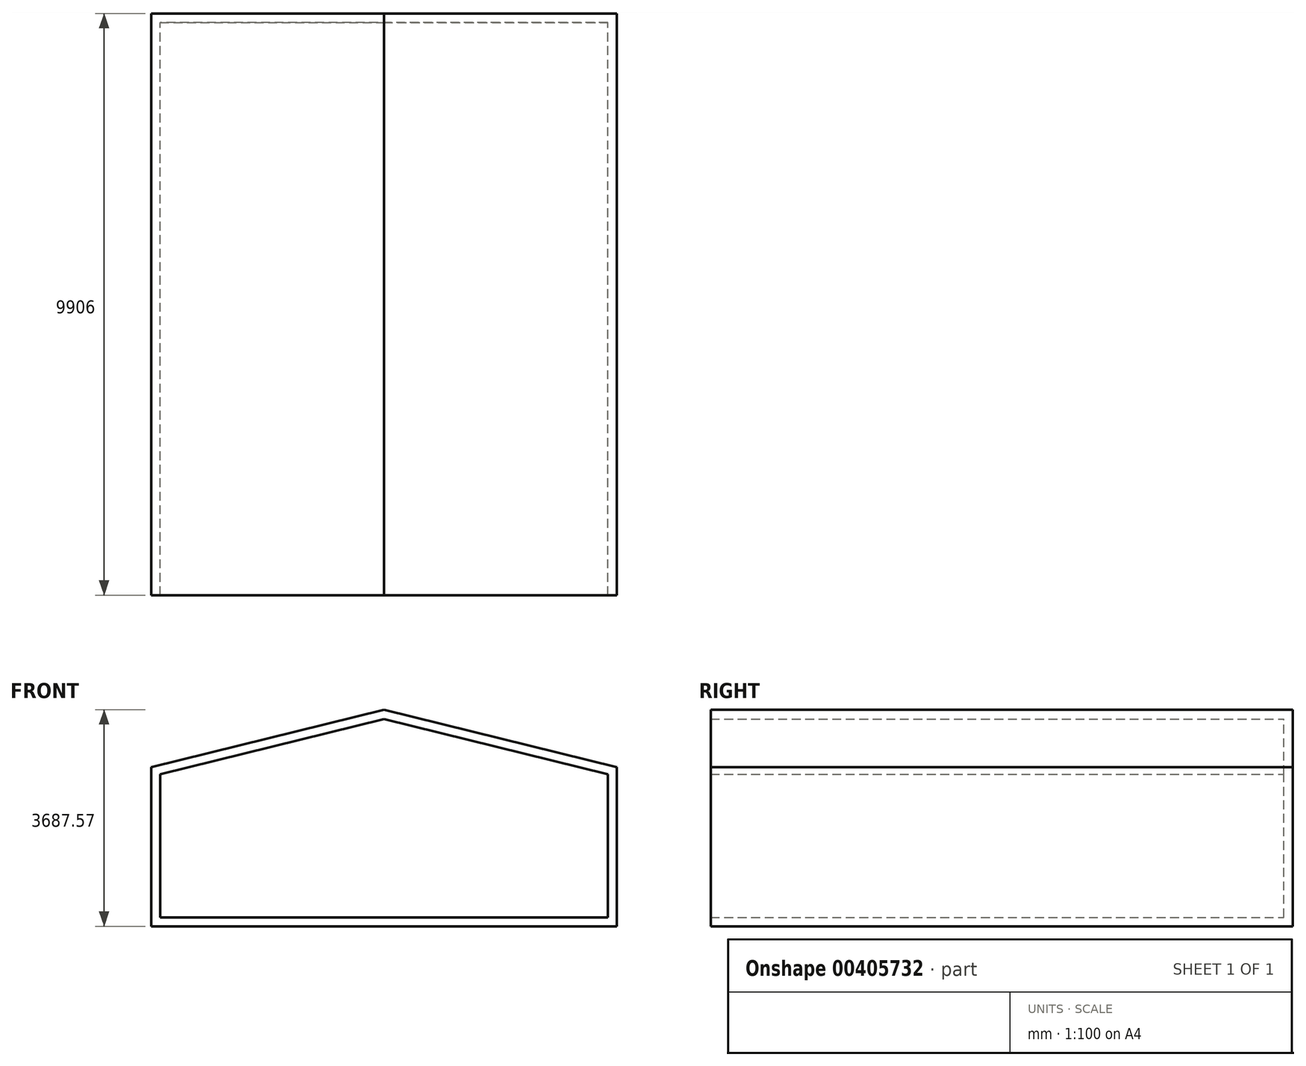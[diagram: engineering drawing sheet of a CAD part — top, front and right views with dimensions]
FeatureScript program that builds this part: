
annotation { "Feature Type Name" : "Feature", "Feature Type Description" : "" }
export const myFeature = defineFeature(function(context is Context, id is Id, definition is map)
    precondition{}
    {
        {
            var Q0;
            Q0=qCreatedBy(makeId("Front.planeOp"),FACE);
            var sketch = newSketch(context, id + "F0", { "sketchPlane" : qUnion([Q0])});
            skLineSegment(sketch, "E0", {"start": v(0, 0) * mm, "end": v(0, 2438.4) * mm});
            skLineSegment(sketch, "E1", {"start": v(0, 2438.4) * mm, "end": v(3810, 3378.2) * mm});
            skLineSegment(sketch, "E2", {"start": v(3810, 3378.2) * mm, "end": v(7620, 2438.4) * mm});
            skLineSegment(sketch, "E3", {"start": v(7620, 2438.4) * mm, "end": v(7620, 0) * mm});
            skLineSegment(sketch, "E4", {"start": v(7620, 0) * mm, "end": v(0, 0) * mm});
            skLineSegment(sketch, "E5.0", {"start": v(3810, 3535.17) * mm, "end": v(7772.4, 2557.78) * mm});
            skLineSegment(sketch, "E5.1", {"start": v(-152.4, 2557.78) * mm, "end": v(3810, 3535.17) * mm});
            skLineSegment(sketch, "E5.2", {"start": v(7772.4, 2557.78) * mm, "end": v(7772.4, -152.4) * mm});
            skLineSegment(sketch, "E5.3", {"start": v(7772.4, -152.4) * mm, "end": v(-152.4, -152.4) * mm});
            skLineSegment(sketch, "E5.4", {"start": v(-152.4, -152.4) * mm, "end": v(-152.4, 2557.78) * mm});
            skSolve(sketch);
        }
        {
            var Q0;
            Q0 = qSketchRegion(id + "F0", true);
            var Q1;
            Q1=makeQuery(id+"F0.imprint","IMPRINT",FACE,{"disambiguationData":[TD([[makeQuery(id+"F0.imprint","IMPRINT",EDGE,{"derivedFrom":sQuery(id+"F0.wireOp",EDGE,"E0")}),-1.0]])]});
            extrude(context, id + "F1", {"entities" : qUnion([Q0, Q1]), "oppositeDirection" : true, "depth" : 152.4 * mm});
        }
        {
            var Q0;
            Q0=makeQuery(id+"F0.imprint","IMPRINT",FACE,{"disambiguationData":[TD([[makeQuery(id+"F0.imprint","IMPRINT",EDGE,{"derivedFrom":sQuery(id+"F0.wireOp",EDGE,"E0")}),1.0]])]});
            extrude(context, id + "F2", {"entities" : qUnion([Q0]), "operationType" : NewBodyOperationType.ADD, "depth" : 9753.6 * mm});
        }
    });
